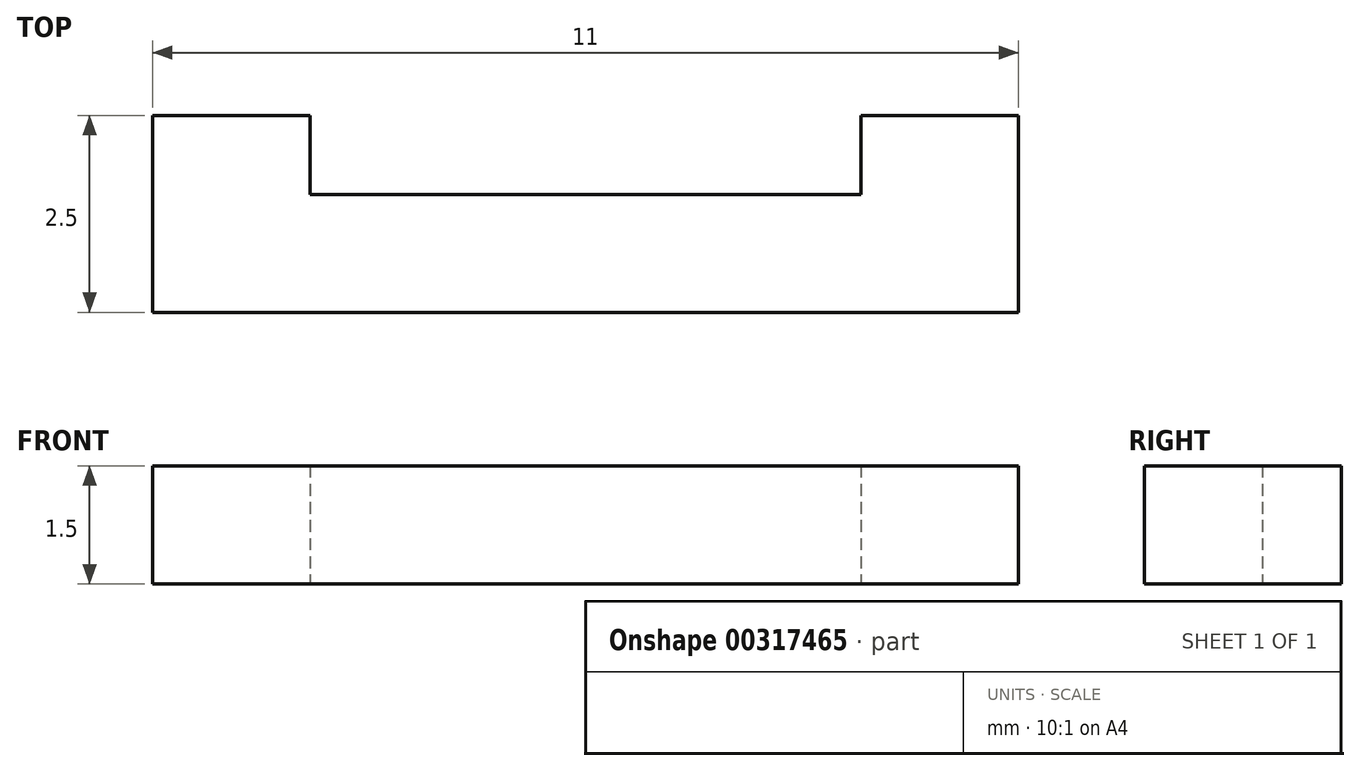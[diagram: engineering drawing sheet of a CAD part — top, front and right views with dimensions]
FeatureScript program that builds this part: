
annotation { "Feature Type Name" : "Feature", "Feature Type Description" : "" }
export const myFeature = defineFeature(function(context is Context, id is Id, definition is map)
    precondition{}
    {
        {
            var Q0;
            Q0=qCreatedBy(makeId("Top.planeOp"),FACE);
            var sketch = newSketch(context, id + "F0", { "sketchPlane" : qUnion([Q0])});
            skLineSegment(sketch, "E0", {"start": v(-5.5, 1) * mm, "end": v(-3.5, 1) * mm});
            skLineSegment(sketch, "E1", {"start": v(-3.5, 1) * mm, "end": v(-3.5, 0) * mm});
            skLineSegment(sketch, "E2", {"start": v(-3.5, 0) * mm, "end": v(3.5, 0) * mm});
            skLineSegment(sketch, "E3", {"start": v(3.5, 0) * mm, "end": v(3.5, 1) * mm});
            skLineSegment(sketch, "E4", {"start": v(3.5, 1) * mm, "end": v(5.5, 1) * mm});
            skLineSegment(sketch, "E5", {"start": v(5.5, 1) * mm, "end": v(5.5, -1.5) * mm});
            skLineSegment(sketch, "E6", {"start": v(5.5, -1.5) * mm, "end": v(-5.5, -1.5) * mm});
            skLineSegment(sketch, "E7", {"start": v(-5.5, -1.5) * mm, "end": v(-5.5, 1) * mm});
            skSolve(sketch);
        }
        {
            var Q0;
            Q0=makeQuery(id+"F0.imprint","IMPRINT",FACE,{"disambiguationData":[TD([[makeQuery(id+"F0.imprint","IMPRINT",EDGE,{"derivedFrom":sQuery(id+"F0.wireOp",EDGE,"E0")}),-1.0]])]});
            extrude(context, id + "F1", {"entities" : qUnion([Q0]), "depth" : 1.5 * mm});
        }
    });
